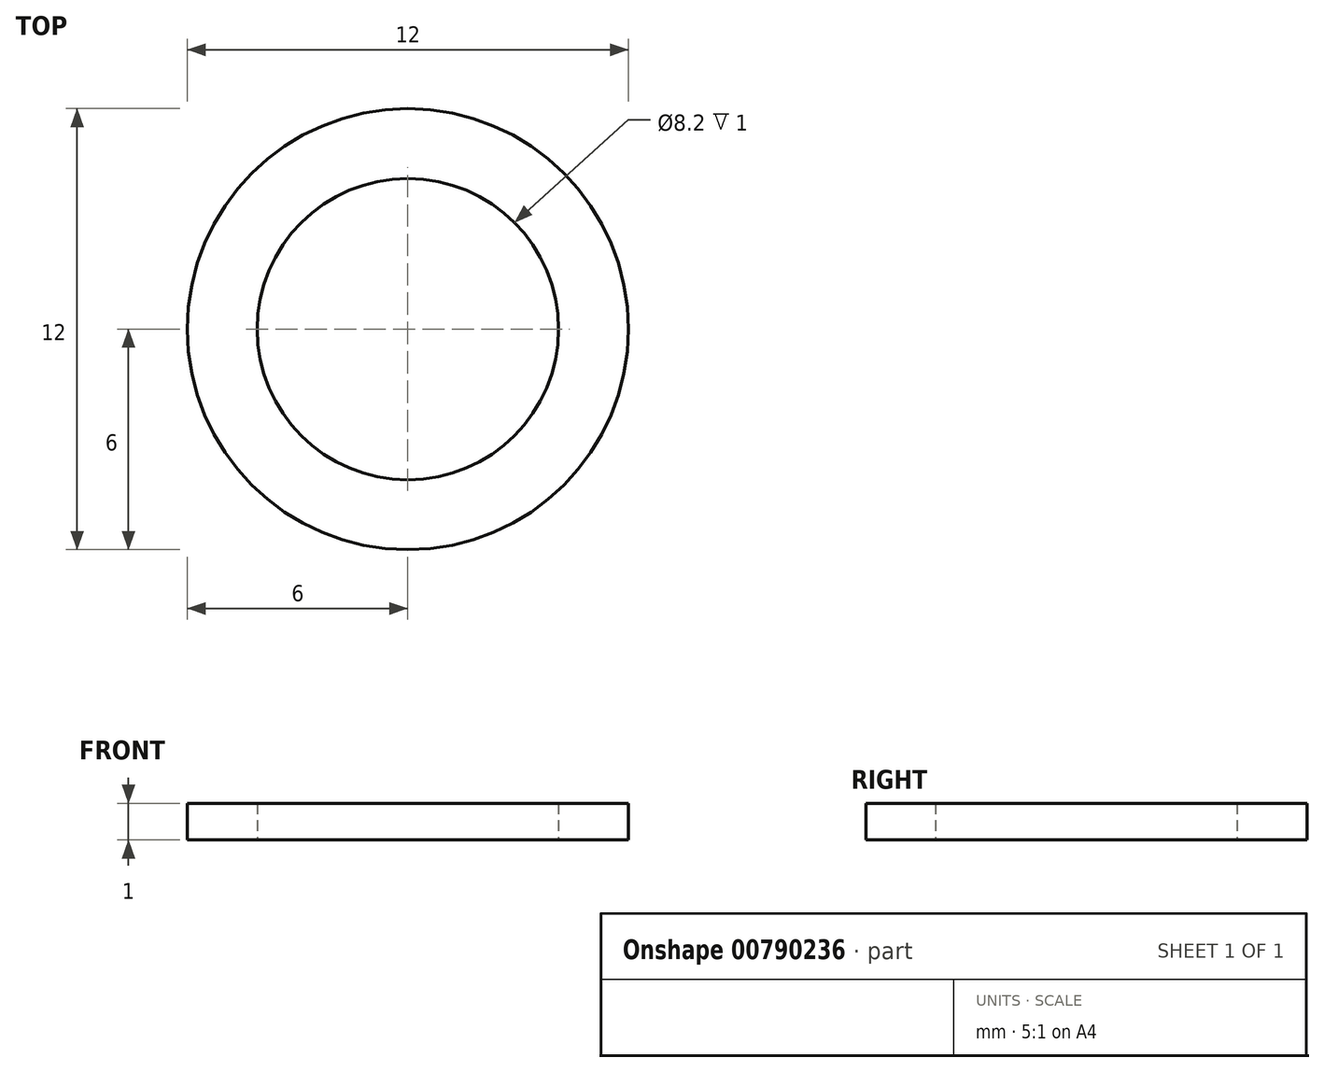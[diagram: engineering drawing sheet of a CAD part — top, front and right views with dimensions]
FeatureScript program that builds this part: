
annotation { "Feature Type Name" : "Feature", "Feature Type Description" : "" }
export const myFeature = defineFeature(function(context is Context, id is Id, definition is map)
    precondition{}
    {
        {
            var Q0;
            Q0=qCreatedBy(makeId("Top.planeOp"),FACE);
            var sketch = newSketch(context, id + "F0", { "sketchPlane" : qUnion([Q0])});
            skCircle(sketch, "E0", {"center": v(0, 0) * mm, "radius": 6 * mm});
            skCircle(sketch, "E1", {"center": v(0, 0) * mm, "radius": 4.1 * mm});
            skSolve(sketch);
        }
        {
            var Q0;
            Q0 = qSketchRegion(id + "F0", true);
            extrude(context, id + "F1", {"entities" : qUnion([Q0]), "depth" : 1 * mm, "offsetDistance" : 25 * mm});
        }
    });
